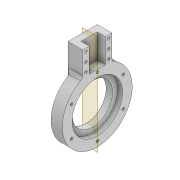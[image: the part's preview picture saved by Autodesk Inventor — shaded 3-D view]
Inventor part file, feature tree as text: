
AUTODESK INVENTOR PART (.ipt)
format: ipt  version: 2022 (Build 260153000, 153)  size: 212,480 bytes
history: native  units: mm
features: extrude x7, sketch x6, fillet x2, pattern_circular x1, plane x1, mirror x1, projected_geometry x1
ambient origin geometry x8: Origin, YZ Plane, XZ Plane, XY Plane, X Axis, Y Axis, Z Axis, Center Point
bodies: Solid1 (feature_tree)
feature tree (19):
  extrude  "Extrusion1"  Depth=12.0mm
  extrude  "Extrusion2"  Depth=8.0mm TaperAngle=0.0deg
  extrude  "Extrusion3"  Depth=6.0mm TaperAngle=0.0deg
  pattern_circular  "Circular Pattern1"  Count=10  [1 undecoded]
  plane  "Work Plane1"
  sketch  "Sketch4"  dims[d8=3.2mm]
  extrude  "Extrusion4"  Depth=5.0mm
  extrude  "Extrusion5"  Depth=10.1mm
  fillet  "Fillet1"  Radius=20.2mm
  extrude  "Extrusion6"  Depth=10.1mm
  fillet  "Fillet2"  Radius=8.0mm
  extrude  "Extrusion7"  Depth=8.0mm
  mirror  "Mirror1"
  sketch  "Sketch1"  dims[d0=62.5mm d1=12.0mm]
  sketch  "Sketch2"  dims[d2=50.0mm d3=8.0mm d4=0.0mm]
  projected_geometry  "Projected Loop1"
  sketch  "Sketch3"  dims[d5=62.5mm d6=6.0mm d7=0.0mm]
  sketch  "Sketch6"  dims[d9=37.0mm d10=100.0mm d11=0.0mm]
  sketch  "Sketch7"  dims[d12=60.0mm d13=360.0deg d15=40.0mm d16=10.1mm d17=20.2mm d18=10.1mm d20=8.0mm d21=8.0mm d22=100.0mm d23=0.0mm d24=30.0mm d25=0.0mm d26=5.0mm d27=3.2mm d28=3.2mm d29=3.2mm d30=4.0mm d31=4.0mm d32=15.0mm d33=4.0mm d34=9.0mm d35=4.0mm d36=0.0mm d37=5.0mm d38=100.0mm d39=0.0mm]
note: 1 required parameter value undecoded (feature->parameter linkage not recoverable at this tier; creation-order binding heuristic only, values carry confidence <= 0.55)
